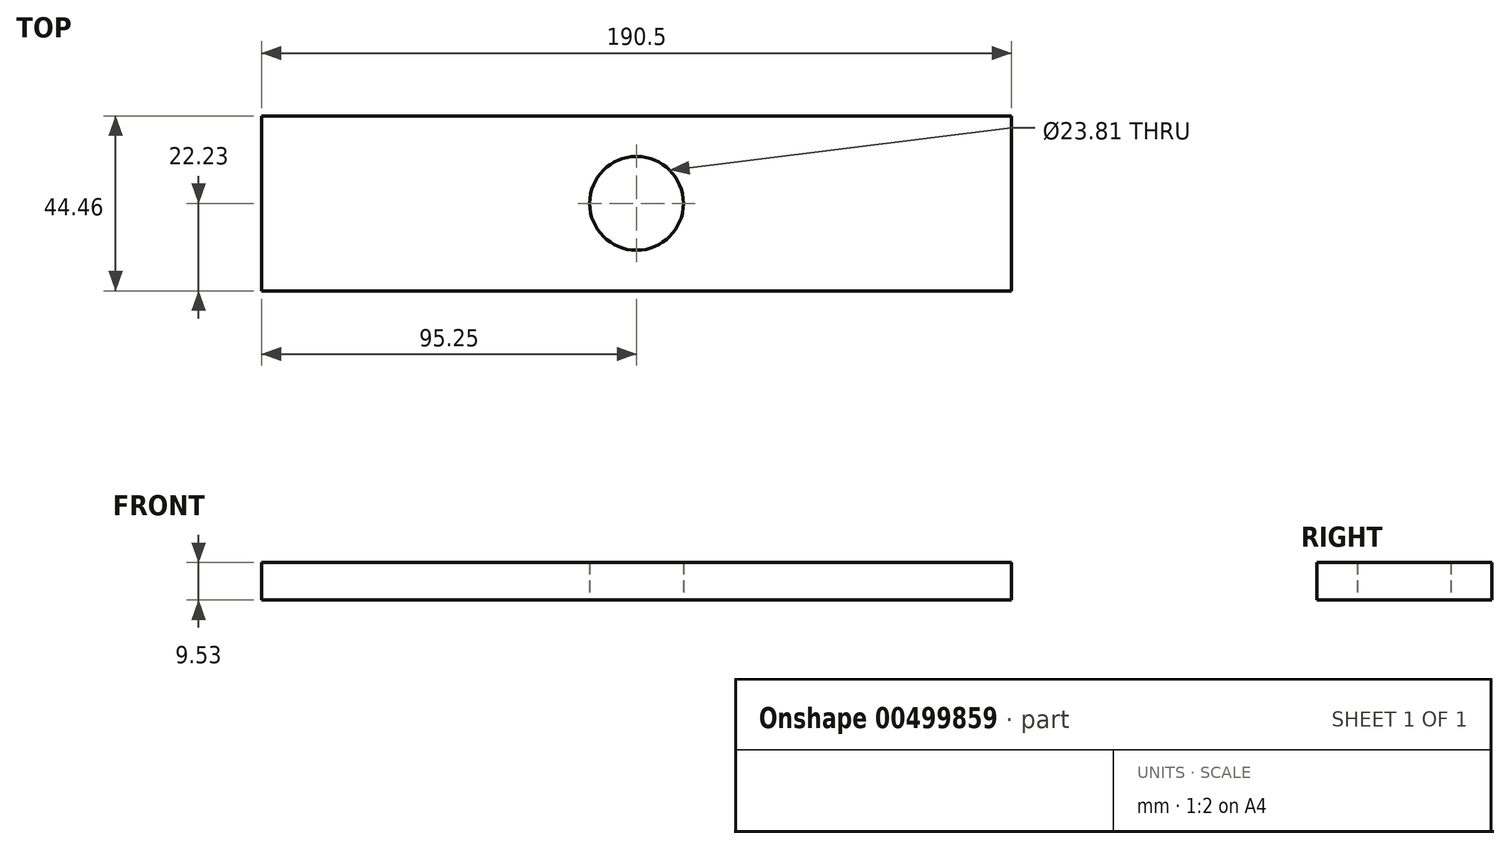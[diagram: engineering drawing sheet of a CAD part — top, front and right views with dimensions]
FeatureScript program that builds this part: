
annotation { "Feature Type Name" : "Feature", "Feature Type Description" : "" }
export const myFeature = defineFeature(function(context is Context, id is Id, definition is map)
    precondition{}
    {
        {
            var Q0;
            Q0=qCreatedBy(makeId("Top.planeOp"),FACE);
            var sketch = newSketch(context, id + "F0", { "sketchPlane" : qUnion([Q0])});
            skLineSegment(sketch, "E0.bottom", {"start": v(95.25, -22.22) * mm, "end": v(-95.25, -22.23) * mm});
            skLineSegment(sketch, "E0.top", {"start": v(95.25, 22.23) * mm, "end": v(-95.25, 22.22) * mm});
            skLineSegment(sketch, "E0.left", {"start": v(95.25, -22.22) * mm, "end": v(95.25, 22.23) * mm});
            skLineSegment(sketch, "E0.right", {"start": v(-95.25, -22.23) * mm, "end": v(-95.25, 22.22) * mm});
            skPoint(sketch, "E0.middle", {"position": v(0, 0) * mm});
            skCircle(sketch, "E1", {"center": v(0, 0) * mm, "radius": 11.9 * mm});
            skSolve(sketch);
        }
        {
            var Q0;
            Q0 = qSketchRegion(id + "F0", true);
            extrude(context, id + "F1", {"entities" : qUnion([Q0]), "depth" : 9.52 * mm});
        }
    });
